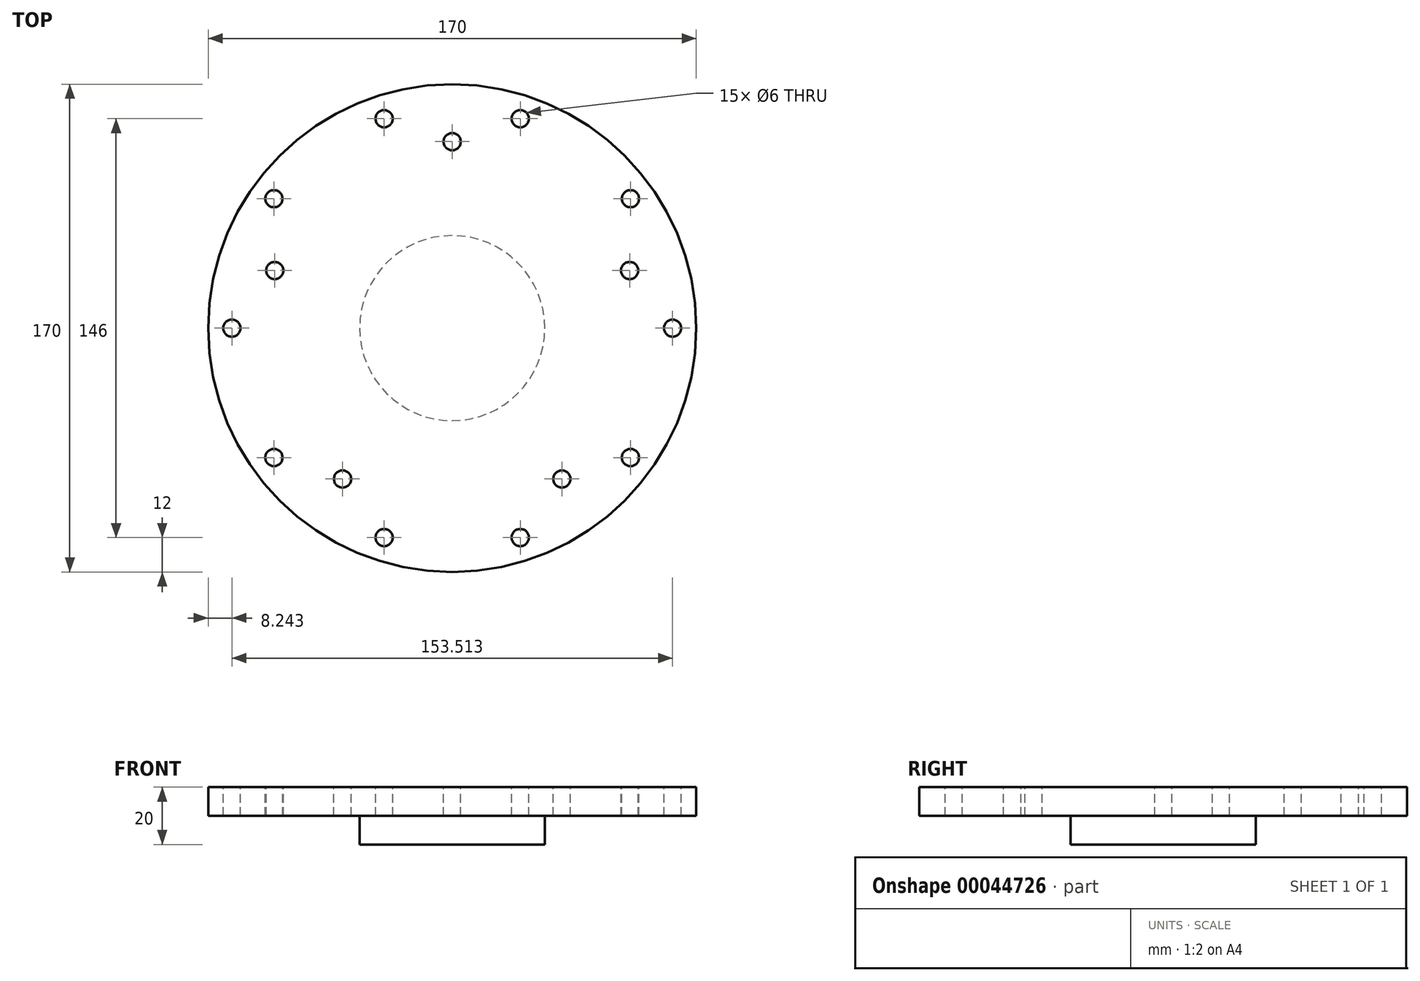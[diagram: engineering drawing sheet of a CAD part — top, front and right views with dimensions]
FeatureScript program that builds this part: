
annotation { "Feature Type Name" : "Feature", "Feature Type Description" : "" }
export const myFeature = defineFeature(function(context is Context, id is Id, definition is map)
    precondition{}
    {
        {
            var Q0;
            Q0=qCreatedBy(makeId("Top.planeOp"),FACE);
            var sketch = newSketch(context, id + "F0", { "sketchPlane" : qUnion([Q0])});
            skCircle(sketch, "E0", {"center": v(0, 0) * mm, "radius": 85 * mm});
            skSolve(sketch);
        }
        {
            var Q0;
            Q0 = qSketchRegion(id + "F0", true);
            extrude(context, id + "F1", {"entities" : qUnion([Q0]), "depth" : 10 * mm});
        }
        {
            var Q0;
            Q0=makeQuery(id+"F1.opExtrude","CAP_FACE",FACE,{"disambiguationData":[OSD([sQuery(id+"F0.wireOp",EDGE,"E0")])],"isStart":true});
            var sketch = newSketch(context, id + "F2", { "sketchPlane" : qUnion([Q0])});
            skCircle(sketch, "E1", {"center": v(0, 0) * mm, "radius": 32.25 * mm});
            skSolve(sketch);
        }
        {
            var Q0;
            Q0 = qSketchRegion(id + "F2", true);
            extrude(context, id + "F3", {"entities" : qUnion([Q0]), "operationType" : NewBodyOperationType.ADD, "depth" : 10 * mm});
        }
        {
            var Q0;
            Q0=makeQuery(id+"F1.opExtrude","CAP_FACE",FACE,{"disambiguationData":[OSD([sQuery(id+"F0.wireOp",EDGE,"E0")])],"isStart":false});
            var sketch = newSketch(context, id + "F4", { "sketchPlane" : qUnion([Q0])});
            skCircle(sketch, "E2", {"center": v(0, 65) * mm, "radius": 3 * mm});
            skCircle(sketch, "E3.1.0", {"center": v(-61.82, 20.09) * mm, "radius": 3 * mm});
            skCircle(sketch, "E3.2.0", {"center": v(-38.2, -52.59) * mm, "radius": 3 * mm});
            skCircle(sketch, "E3.3.0", {"center": v(38.2, -52.59) * mm, "radius": 3 * mm});
            skCircle(sketch, "E3.4.0", {"center": v(61.82, 20.09) * mm, "radius": 3 * mm});
            skPoint(sketch, "E3.center", {"position": v(0, 0) * mm});
            skSolve(sketch);
        }
        {
            var Q0;
            Q0 = qSketchRegion(id + "F4", true);
            extrude(context, id + "F5", {"entities" : qUnion([Q0]), "operationType" : NewBodyOperationType.REMOVE, "endBound" : BoundingType.THROUGH_ALL, "oppositeDirection" : true, "depth" : 25 * mm});
        }
        {
            var Q0;
            Q0=makeQuery(id+"F1.opExtrude","CAP_FACE",FACE,{"disambiguationData":[OSD([sQuery(id+"F0.wireOp",EDGE,"E0")])],"isStart":false});
            var sketch = newSketch(context, id + "F6", { "sketchPlane" : qUnion([Q0])});
            skCircle(sketch, "E4", {"center": v(-23.72, -73) * mm, "radius": 3 * mm});
            skLineSegment(sketch, "E5", {"start": v(0, 0) * mm, "end": v(-23.72, -73) * mm, "construction": true});
            skCircle(sketch, "E6.1.0", {"center": v(23.72, -73) * mm, "radius": 3 * mm});
            skCircle(sketch, "E6.2.0", {"center": v(62.1, -45.12) * mm, "radius": 3 * mm});
            skCircle(sketch, "E6.3.0", {"center": v(76.76, 0) * mm, "radius": 3 * mm});
            skCircle(sketch, "E6.4.0", {"center": v(62.1, 45.12) * mm, "radius": 3 * mm});
            skCircle(sketch, "E6.5.0", {"center": v(23.72, 73) * mm, "radius": 3 * mm});
            skCircle(sketch, "E6.6.0", {"center": v(-23.72, 73) * mm, "radius": 3 * mm});
            skCircle(sketch, "E6.7.0", {"center": v(-62.1, 45.12) * mm, "radius": 3 * mm});
            skCircle(sketch, "E6.8.0", {"center": v(-76.76, 0) * mm, "radius": 3 * mm});
            skCircle(sketch, "E6.9.0", {"center": v(-62.1, -45.12) * mm, "radius": 3 * mm});
            skPoint(sketch, "E6.center", {"position": v(0, 0) * mm});
            skSolve(sketch);
        }
        {
            var Q0;
            Q0 = qSketchRegion(id + "F6", true);
            extrude(context, id + "F7", {"entities" : qUnion([Q0]), "operationType" : NewBodyOperationType.REMOVE, "endBound" : BoundingType.THROUGH_ALL, "oppositeDirection" : true, "depth" : 25 * mm});
        }
    });
